# Revit family: EKF_EE_Поперечный профиль(4шт)_EKF_AVERES
name_source: partatom
category: Электрооборудование
units: mm (PartAtom-declared; Revit-internal decimal feet)

## family parameters
Всегда вертикально = Нет
На основе рабочей плоскости = Да
Общий = Да
При загрузке вырезать с полостями = Нет
Размер круглого соединителя = Использовать диаметр
Тип детали = Силовой щит
Точка расчета площади = Нет

## types (4) — shared parameters
ADSK_Единица измерения = шт.
ADSK_Завод-изготовитель = EKF
ADSK_Количество = 1
ADSK_Марка = Поперечный профиль
ADSK_Материал = RAL 7035_Сталь
ADSK_Обозначение = Поперечный профиль
ADSK_Размер_Высота = 43 мм
ADSK_Размер_Глубина = 43 мм
Изготовитель = EKF
Серия номенклатуры = Averes
Степень защиты IP = -
ТВ = EKF_2_TRIVIA_AVERES
Тип установки = -
zero-valued in all types: ADSK_Масса, Отметка по умолчанию

## per-type parameters (varying)
| type | ADSK_Код изделия | ADSK_Наименование | ADSK_Размер_Ширина | Тип |
| Поперечный профиль Ш800 (4шт) EKF AVERES | FCM800 | Поперечный профиль Ш800 (4 шт) EKF AVERES | 725 мм | 398 мм |
| Поперечный профиль Ш600 (4шт) EKF AVERES | FCM600 | Поперечный профиль Ш600 (4 шт) EKF AVERES | 525 мм | 397 мм |
| Поперечный профиль Ш400 (4шт) EKF AVERES | FCM400 | Поперечный профиль Ш400 (4 шт) EKF AVERES | 325 мм | 396 мм |
| Поперечный профиль Ш300 (4шт) EKF AVERES | FCM300 | Поперечный профиль Ш300 (4 шт) EKF AVERES | 225 мм | 395 мм |
